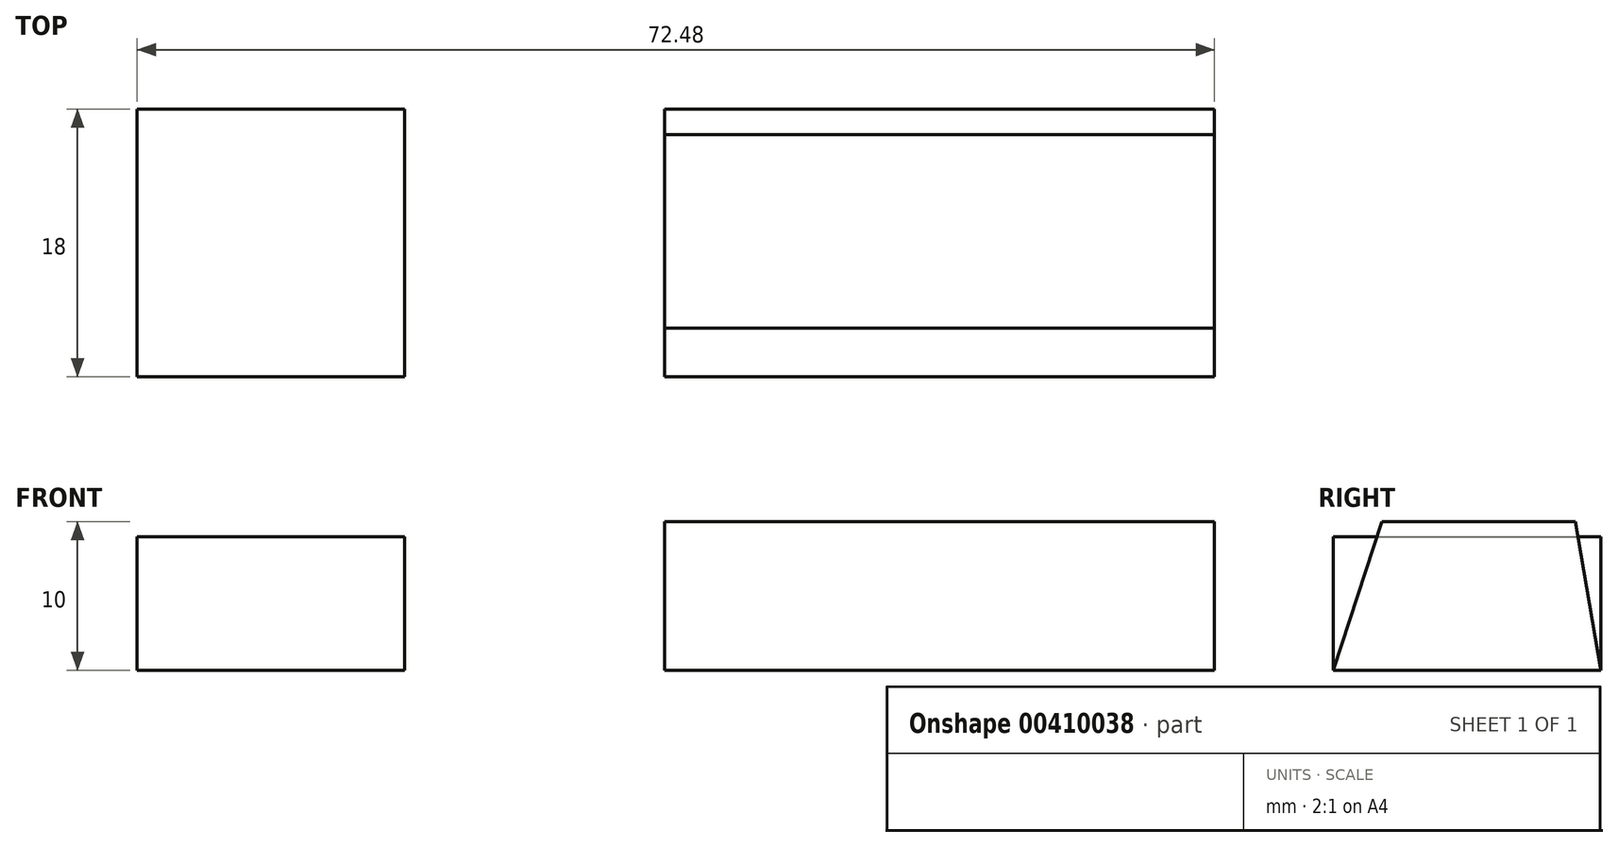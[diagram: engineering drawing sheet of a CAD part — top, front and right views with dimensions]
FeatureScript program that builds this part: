
annotation { "Feature Type Name" : "Feature", "Feature Type Description" : "" }
export const myFeature = defineFeature(function(context is Context, id is Id, definition is map)
    precondition{}
    {
        {
            var Q0;
            Q0=qCreatedBy(makeId("Top.planeOp"),FACE);
            var sketch = newSketch(context, id + "F0", { "sketchPlane" : qUnion([Q0])});
            skLineSegment(sketch, "E0.bottom", {"start": v(0, 0) * mm, "end": v(37, 0) * mm});
            skLineSegment(sketch, "E0.top", {"start": v(0, 18) * mm, "end": v(37, 18) * mm});
            skLineSegment(sketch, "E0.left", {"start": v(0, 0) * mm, "end": v(0, 18) * mm});
            skLineSegment(sketch, "E0.right", {"start": v(37, 0) * mm, "end": v(37, 18) * mm});
            skSolve(sketch);
        }
        {
            var Q0;
            Q0=makeQuery(id+"F0.imprint","IMPRINT",FACE,{"disambiguationData":[TD([[makeQuery(id+"F0.imprint","IMPRINT",EDGE,{"derivedFrom":sQuery(id+"F0.wireOp",EDGE,"E0.bottom")}),1.0]])]});
            extrude(context, id + "F1", {"entities" : qUnion([Q0]), "depth" : 10 * mm});
        }
        {
            var Q0;
            Q0=makeQuery(id+"F1.opExtrude","SWEPT_FACE",FACE,{"disambiguationData":[OSD([sQuery(id+"F0.wireOp",EDGE,"E0.right")])]});
            var sketch = newSketch(context, id + "F2", { "sketchPlane" : qUnion([Q0])});
            skLineSegment(sketch, "E1", {"start": v(0, 0) * mm, "end": v(3.27, 10) * mm});
            skLineSegment(sketch, "E2", {"start": v(3.27, 10) * mm, "end": v(16.3, 10) * mm});
            skLineSegment(sketch, "E3", {"start": v(16.3, 10) * mm, "end": v(18, 0) * mm});
            skLineSegment(sketch, "E4", {"start": v(18, 0) * mm, "end": v(0, 0) * mm});
            skSolve(sketch);
        }
        {
            var Q0;
            {var subQ2=sQuery(id+"F2.wireOp",EDGE,"E1");Q0=makeQuery(id+"F2.imprint","IMPRINT",FACE,{"disambiguationData":[TD([[makeQuery(id+"F2.imprint","IMPRINT",EDGE,{"derivedFrom":subQ2}),1.0]])]});}
            var Q1;
            {var subQ2=sQuery(id+"F2.wireOp",EDGE,"E3");Q1=makeQuery(id+"F2.imprint","IMPRINT",FACE,{"disambiguationData":[TD([[makeQuery(id+"F2.imprint","IMPRINT",EDGE,{"derivedFrom":subQ2}),1.0]])]});}
            extrude(context, id + "F3", {"entities" : qUnion([Q0, Q1]), "operationType" : NewBodyOperationType.REMOVE, "oppositeDirection" : true, "depth" : 50.62 * mm});
        }
        {
            var Q0;
            Q0=qCreatedBy(makeId("Top.planeOp"),FACE);
            var sketch = newSketch(context, id + "F4", { "sketchPlane" : qUnion([Q0])});
            skLineSegment(sketch, "E5.bottom", {"start": v(-17.48, 0) * mm, "end": v(-35.48, 0) * mm});
            skLineSegment(sketch, "E5.top", {"start": v(-17.48, 18) * mm, "end": v(-35.48, 18) * mm});
            skLineSegment(sketch, "E5.left", {"start": v(-17.48, 0) * mm, "end": v(-17.48, 18) * mm});
            skLineSegment(sketch, "E5.right", {"start": v(-35.48, 0) * mm, "end": v(-35.48, 18) * mm});
            skSolve(sketch);
        }
        {
            var Q0;
            Q0=qSketchRegion(id+"F4",true);
            extrude(context, id + "F5", {"entities" : qUnion([Q0]), "depth" : 9 * mm});
        }
    });
